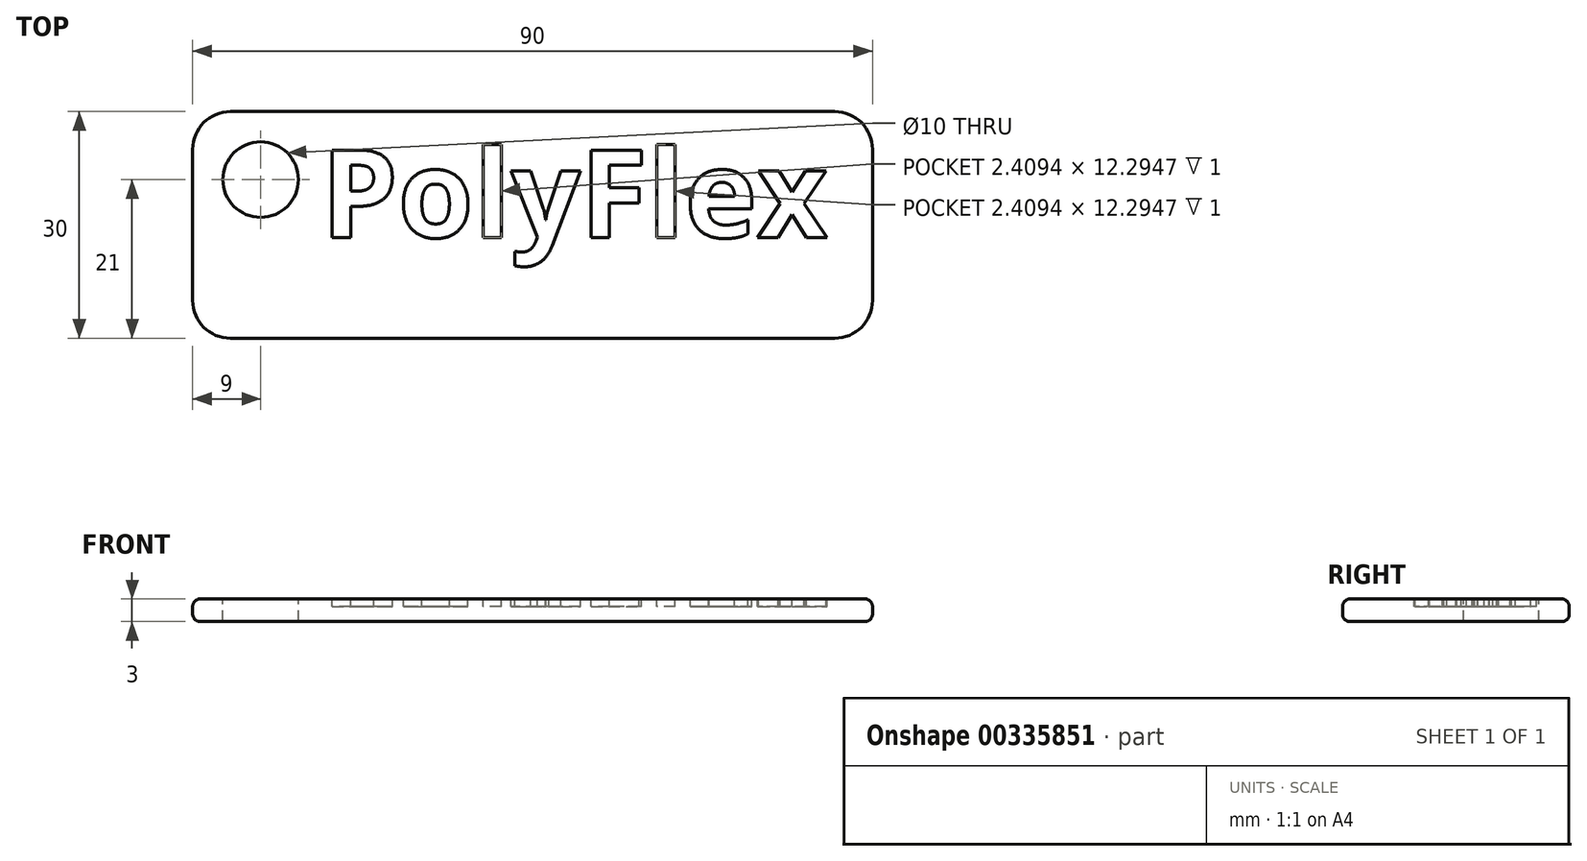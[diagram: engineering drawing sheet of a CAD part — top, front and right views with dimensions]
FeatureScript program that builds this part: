
annotation { "Feature Type Name" : "Feature", "Feature Type Description" : "" }
export const myFeature = defineFeature(function(context is Context, id is Id, definition is map)
    precondition{}
    {
        {
            var Q0;
            Q0=qCreatedBy(makeId("Top.planeOp"),FACE);
            var sketch = newSketch(context, id + "F0", { "sketchPlane" : qUnion([Q0])});
            skLineSegment(sketch, "E0.bottom", {"start": v(-45, 15) * mm, "end": v(45, 15) * mm});
            skLineSegment(sketch, "E0.top", {"start": v(-45, -15) * mm, "end": v(45, -15) * mm});
            skLineSegment(sketch, "E0.left", {"start": v(-45, 15) * mm, "end": v(-45, -15) * mm});
            skLineSegment(sketch, "E0.right", {"start": v(45, 15) * mm, "end": v(45, -15) * mm});
            skLineSegment(sketch, "E1", {"start": v(-45, 15) * mm, "end": v(45, -15) * mm, "construction": true});
            skSolve(sketch);
        }
        {
            var Q0;
            Q0=makeQuery(id+"F0.imprint","IMPRINT",FACE,{"disambiguationData":[TD([[makeQuery(id+"F0.imprint","IMPRINT",EDGE,{"derivedFrom":sQuery(id+"F0.wireOp",EDGE,"E0.bottom")}),-1.0]])]});
            extrude(context, id + "F1", {"entities" : qUnion([Q0]), "depth" : 3 * mm});
        }
        {
            var Q0;
            Q0=makeQuery(id+"F1.opExtrude","CAP_FACE",FACE,{"disambiguationData":[OSD([sQuery(id+"F0.wireOp",EDGE,"E0.bottom"),sQuery(id+"F0.wireOp",EDGE,"E0.top"),sQuery(id+"F0.wireOp",EDGE,"E0.left"),sQuery(id+"F0.wireOp",EDGE,"E0.right")])],"isStart":false});
            var Q1;
            Q1=makeQuery(id+"F1.opExtrude","CAP_FACE",FACE,{"disambiguationData":[OSD([sQuery(id+"F0.wireOp",EDGE,"E0.bottom"),sQuery(id+"F0.wireOp",EDGE,"E0.top"),sQuery(id+"F0.wireOp",EDGE,"E0.left"),sQuery(id+"F0.wireOp",EDGE,"E0.right")])],"isStart":true});
            fillet(context, id + "F2", {"entities" : qUnion([Q0, Q1]), "radius" : 1 * mm, "tangentPropagation" : true, "allowEdgeOverflow" : false});
        }
        {
            var Q0;
            Q0=makeQuery(id+"F1.opExtrude","SWEPT_EDGE",EDGE,{"disambiguationData":[OSD([sQuery(id+"F0.wireOp",EDGE,"E0.top"),sQuery(id+"F0.wireOp",EDGE,"E0.right")])]});
            var Q1;
            Q1=makeQuery(id+"F1.opExtrude","SWEPT_EDGE",EDGE,{"disambiguationData":[OSD([sQuery(id+"F0.wireOp",EDGE,"E0.bottom"),sQuery(id+"F0.wireOp",EDGE,"E0.right")])]});
            var Q2;
            Q2=makeQuery(id+"F1.opExtrude","SWEPT_EDGE",EDGE,{"disambiguationData":[OSD([sQuery(id+"F0.wireOp",EDGE,"E0.bottom"),sQuery(id+"F0.wireOp",EDGE,"E0.left")])]});
            var Q3;
            Q3=makeQuery(id+"F1.opExtrude","SWEPT_EDGE",EDGE,{"disambiguationData":[OSD([sQuery(id+"F0.wireOp",EDGE,"E0.top"),sQuery(id+"F0.wireOp",EDGE,"E0.left")])]});
            fillet(context, id + "F3", {"entities" : qUnion([Q0, Q1, Q2, Q3]), "radius" : 5 * mm, "tangentPropagation" : true, "allowEdgeOverflow" : false});
        }
        {
            var Q0;
            {var subQ0=sQuery(id+"F0.wireOp",EDGE,"E0.left");var subQ2=sQuery(id+"F0.wireOp",EDGE,"E0.bottom");var subQ4=sQuery(id+"F0.wireOp",EDGE,"E0.right");var subQ6=sQuery(id+"F0.wireOp",EDGE,"E0.top");Q0=makeQuery(id+"FmQCBBX3Ub0qneL_1.boolean.opBoolean","SPLIT",FACE,{"disambiguationData":[TD([makeQuery(id+"FmQCBBX3Ub0qneL_1.opExtrude","SWEPT_FACE",FACE,{"disambiguationData":[OSD([sQuery(id+"FOCoeRmDbjhRCuz_1.wireOp",EDGE,"4a1fb44a-e7be-4e23-9449-000d953c446c.sketch_text.stroke-0")])]})])],"derivedFrom":makeQuery(id+"F1.opExtrude","CAP_FACE",FACE,{"disambiguationData":[OSD([subQ2,subQ6,subQ0,subQ4])],"isStart":false})});}
            var sketch = newSketch(context, id + "F4", { "sketchPlane" : qUnion([Q0])});
            skCircle(sketch, "E2", {"center": v(-36, 6) * mm, "radius": 5 * mm});
            skSolve(sketch);
        }
        {
            var Q0;
            Q0=qSketchRegion(id+"F4",true);
            extrude(context, id + "F5", {"entities" : qUnion([Q0]), "operationType" : NewBodyOperationType.REMOVE, "oppositeDirection" : true, "depth" : 3 * mm});
        }
        {
            var Q0;
            Q0=makeQuery(id+"F1.opExtrude","CAP_FACE",FACE,{"disambiguationData":[OSD([sQuery(id+"F0.wireOp",EDGE,"E0.bottom"),sQuery(id+"F0.wireOp",EDGE,"E0.top"),sQuery(id+"F0.wireOp",EDGE,"E0.left"),sQuery(id+"F0.wireOp",EDGE,"E0.right")])],"isStart":false});
            var sketch = newSketch(context, id + "F6", { "sketchPlane" : qUnion([Q0])});
            skText(sketch, "E3", { "text": "PolyFlex", "fontName": "OpenSans-Bold.ttf"});
            const initialGuessF6  = {"E3": [-0.028, -0.00165, 1, 0, 0.01165]};
            skSetInitialGuess(sketch, initialGuessF6);
            skSolve(sketch);
        }
        {
            var Q0;
            Q0=qSketchRegion(id+"F6",true);
            extrude(context, id + "F7", {"entities" : qUnion([Q0]), "operationType" : NewBodyOperationType.REMOVE, "oppositeDirection" : true, "depth" : 1 * mm});
        }
    });
